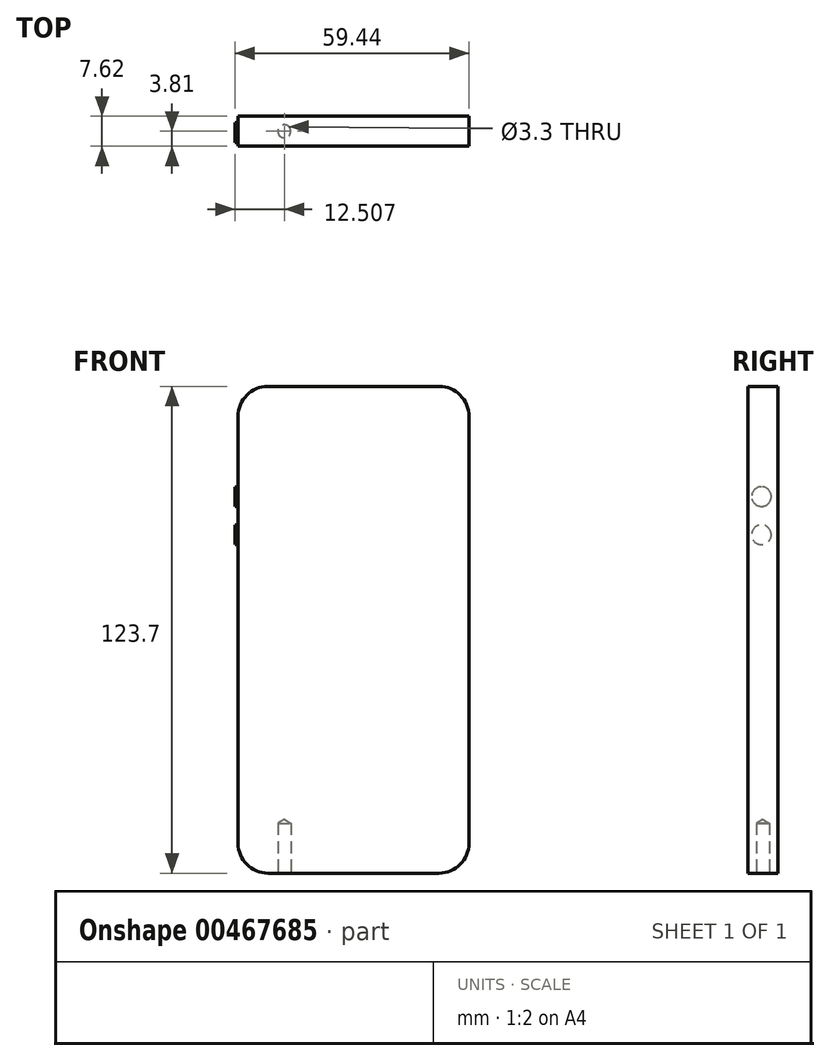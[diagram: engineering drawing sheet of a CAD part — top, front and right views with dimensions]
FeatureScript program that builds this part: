
annotation { "Feature Type Name" : "Feature", "Feature Type Description" : "" }
export const myFeature = defineFeature(function(context is Context, id is Id, definition is map)
    precondition{}
    {
        {
            var Q0;
            Q0=qCreatedBy(makeId("Front.planeOp"),FACE);
            var sketch = newSketch(context, id + "F0", { "sketchPlane" : qUnion([Q0])});
            skLineSegment(sketch, "E0.bottom", {"start": v(-29.34, 61.85) * mm, "end": v(29.34, 61.85) * mm});
            skLineSegment(sketch, "E0.top", {"start": v(-29.34, -61.85) * mm, "end": v(29.34, -61.85) * mm});
            skLineSegment(sketch, "E0.left", {"start": v(-29.34, 61.85) * mm, "end": v(-29.34, -61.85) * mm});
            skLineSegment(sketch, "E0.right", {"start": v(29.34, 61.85) * mm, "end": v(29.34, -61.85) * mm});
            skPoint(sketch, "E0.middle", {"position": v(0, 0) * mm});
            skLineSegment(sketch, "E1.bottom", {"start": v(-25.8, 45.12) * mm, "end": v(25.8, 45.12) * mm});
            skLineSegment(sketch, "E1.top", {"start": v(-25.8, -45.12) * mm, "end": v(25.8, -45.12) * mm});
            skLineSegment(sketch, "E1.left", {"start": v(-25.8, 45.12) * mm, "end": v(-25.8, -45.12) * mm});
            skLineSegment(sketch, "E1.right", {"start": v(25.8, 45.12) * mm, "end": v(25.8, -45.12) * mm});
            skSolve(sketch);
        }
        {
            var Q0;
            Q0=makeQuery(id+"F0.imprint","IMPRINT",FACE,{"disambiguationData":[TD([[makeQuery(id+"F0.imprint","IMPRINT",EDGE,{"derivedFrom":sQuery(id+"F0.wireOp",EDGE,"E0.bottom")}),-1.0]])]});
            extrude(context, id + "F1", {"entities" : qUnion([Q0]), "depth" : 7.62 * mm});
        }
        {
            var Q0;
            Q0=makeQuery(id+"F0.imprint","IMPRINT",FACE,{"disambiguationData":[TD([[makeQuery(id+"F0.imprint","IMPRINT",EDGE,{"derivedFrom":sQuery(id+"F0.wireOp",EDGE,"E1.bottom")}),-1.0]])]});
            extrude(context, id + "F2", {"entities" : qUnion([Q0]), "operationType" : NewBodyOperationType.ADD, "depth" : 7.62 * mm});
        }
        {
            var Q0;
            Q0=makeQuery(id+"F1.opExtrude","SWEPT_EDGE",EDGE,{"disambiguationData":[OSD([sQuery(id+"F0.wireOp",EDGE,"E0.bottom"),sQuery(id+"F0.wireOp",EDGE,"E0.right")])]});
            var Q1;
            Q1=makeQuery(id+"F1.opExtrude","SWEPT_EDGE",EDGE,{"disambiguationData":[OSD([sQuery(id+"F0.wireOp",EDGE,"E0.top"),sQuery(id+"F0.wireOp",EDGE,"E0.right")])]});
            var Q2;
            Q2=makeQuery(id+"F1.opExtrude","SWEPT_EDGE",EDGE,{"disambiguationData":[OSD([sQuery(id+"F0.wireOp",EDGE,"E0.top"),sQuery(id+"F0.wireOp",EDGE,"E0.left")])]});
            var Q3;
            Q3=makeQuery(id+"F1.opExtrude","SWEPT_EDGE",EDGE,{"disambiguationData":[OSD([sQuery(id+"F0.wireOp",EDGE,"E0.bottom"),sQuery(id+"F0.wireOp",EDGE,"E0.left")])]});
            fillet(context, id + "F3", {"entities" : qUnion([Q0, Q1, Q2, Q3]), "radius" : 7.62 * mm, "tangentPropagation" : true, "allowEdgeOverflow" : false});
        }
        {
            var Q0;
            Q0=makeQuery(id+"F1.opExtrude","SWEPT_FACE",FACE,{"disambiguationData":[OSD([sQuery(id+"F0.wireOp",EDGE,"E0.left")])]});
            var sketch = newSketch(context, id + "F4", { "sketchPlane" : qUnion([Q0])});
            skCircle(sketch, "E2", {"center": v(4.18, 24.13) * mm, "radius": 2.5 * mm});
            skCircle(sketch, "E3", {"center": v(4.15, 33.84) * mm, "radius": 2.5 * mm});
            skLineSegment(sketch, "E4.bottom", {"start": v(2.38, 50.25) * mm, "end": v(5.89, 50.25) * mm});
            skLineSegment(sketch, "E4.top", {"start": v(2.38, 42.17) * mm, "end": v(5.89, 42.17) * mm});
            skLineSegment(sketch, "E4.left", {"start": v(2.38, 50.25) * mm, "end": v(2.38, 42.17) * mm});
            skLineSegment(sketch, "E4.right", {"start": v(5.89, 50.25) * mm, "end": v(5.89, 42.17) * mm});
            skPoint(sketch, "E4.middle", {"position": v(4.14, 46.2) * mm});
            skSolve(sketch);
        }
        {
            var Q0;
            Q0=makeQuery(id+"F4.imprint","IMPRINT",FACE,{"disambiguationData":[TD([[makeQuery(id+"F4.imprint","IMPRINT",EDGE,{"derivedFrom":sQuery(id+"F4.wireOp",EDGE,"E2")}),1.0]])]});
            extrude(context, id + "F5", {"entities" : qUnion([Q0]), "operationType" : NewBodyOperationType.ADD, "depth" : 0.76 * mm});
        }
        {
            var Q0;
            Q0=makeQuery(id+"F4.imprint","IMPRINT",FACE,{"disambiguationData":[TD([[makeQuery(id+"F4.imprint","IMPRINT",EDGE,{"derivedFrom":sQuery(id+"F4.wireOp",EDGE,"E3")}),1.0]])]});
            extrude(context, id + "F6", {"entities" : qUnion([Q0]), "operationType" : NewBodyOperationType.ADD, "depth" : 0.76 * mm});
        }
        {
            var Q0;
            Q0=makeQuery(id+"F4.imprint","IMPRINT",FACE,{"disambiguationData":[TD([[makeQuery(id+"F4.imprint","IMPRINT",EDGE,{"derivedFrom":sQuery(id+"F4.wireOp",EDGE,"E4.bottom")}),-1.0]])]});
            extrude(context, id + "F7", {"entities" : qUnion([Q0]), "operationType" : NewBodyOperationType.ADD, "depth" : -2.54 * mm});
        }
        {
            var Q0;
            Q0=makeQuery(id+"F1.opExtrude","SWEPT_FACE",FACE,{"disambiguationData":[OSD([sQuery(id+"F0.wireOp",EDGE,"E0.top")])]});
            var sketch = newSketch(context, id + "F8", { "sketchPlane" : qUnion([Q0])});
            skCircle(sketch, "E5", {"center": v(-17.6, 3.81) * mm, "radius": 1.87 * mm});
            skPoint(sketch, "E5.centerSnap0", {"position": v(-21.72, 3.81) * mm});
            skSolve(sketch);
        }
        {
            var Q0;
            Q0=makeQuery(id+"F8.imprint","IMPRINT",FACE,{"disambiguationData":[TD([[makeQuery(id+"F8.imprint","IMPRINT",EDGE,{"derivedFrom":sQuery(id+"F8.wireOp",EDGE,"E5")}),1.0]])]});
            extrude(context, id + "F9", {"entities" : qUnion([Q0]), "operationType" : NewBodyOperationType.ADD, "oppositeDirection" : true, "depth" : 11.43 * mm});
        }
        {
            var Q0;
            Q0=sQuery(id+"F8.wireOp",VERTEX,"E5.center");
            var Q1;
            Q1=makeQuery(id+"F1.opExtrude","SWEPT_BODY",BODY,{"disambiguationData":[OSD([sQuery(id+"F0.wireOp",EDGE,"E0.bottom"),sQuery(id+"F0.wireOp",EDGE,"E0.top"),sQuery(id+"F0.wireOp",EDGE,"E0.left"),sQuery(id+"F0.wireOp",EDGE,"E0.right"),sQuery(id+"F0.wireOp",EDGE,"E1.bottom"),sQuery(id+"F0.wireOp",EDGE,"E1.top"),sQuery(id+"F0.wireOp",EDGE,"E1.left"),sQuery(id+"F0.wireOp",EDGE,"E1.right")])]});
            hole(context, id + "F10", {"style" : HoleStyle.SIMPLE, "endStyle" : HoleEndStyle.BLIND, "holeDiameter" : 3.3 * mm, "holeDepth" : 12.7 * mm, "isTappedThrough" : true, "tappedDepth" : 12.7 * mm, "tapClearance" : 3, "locations" : qUnion([Q0]), "scope" : qUnion([Q1])});
        }
    });
